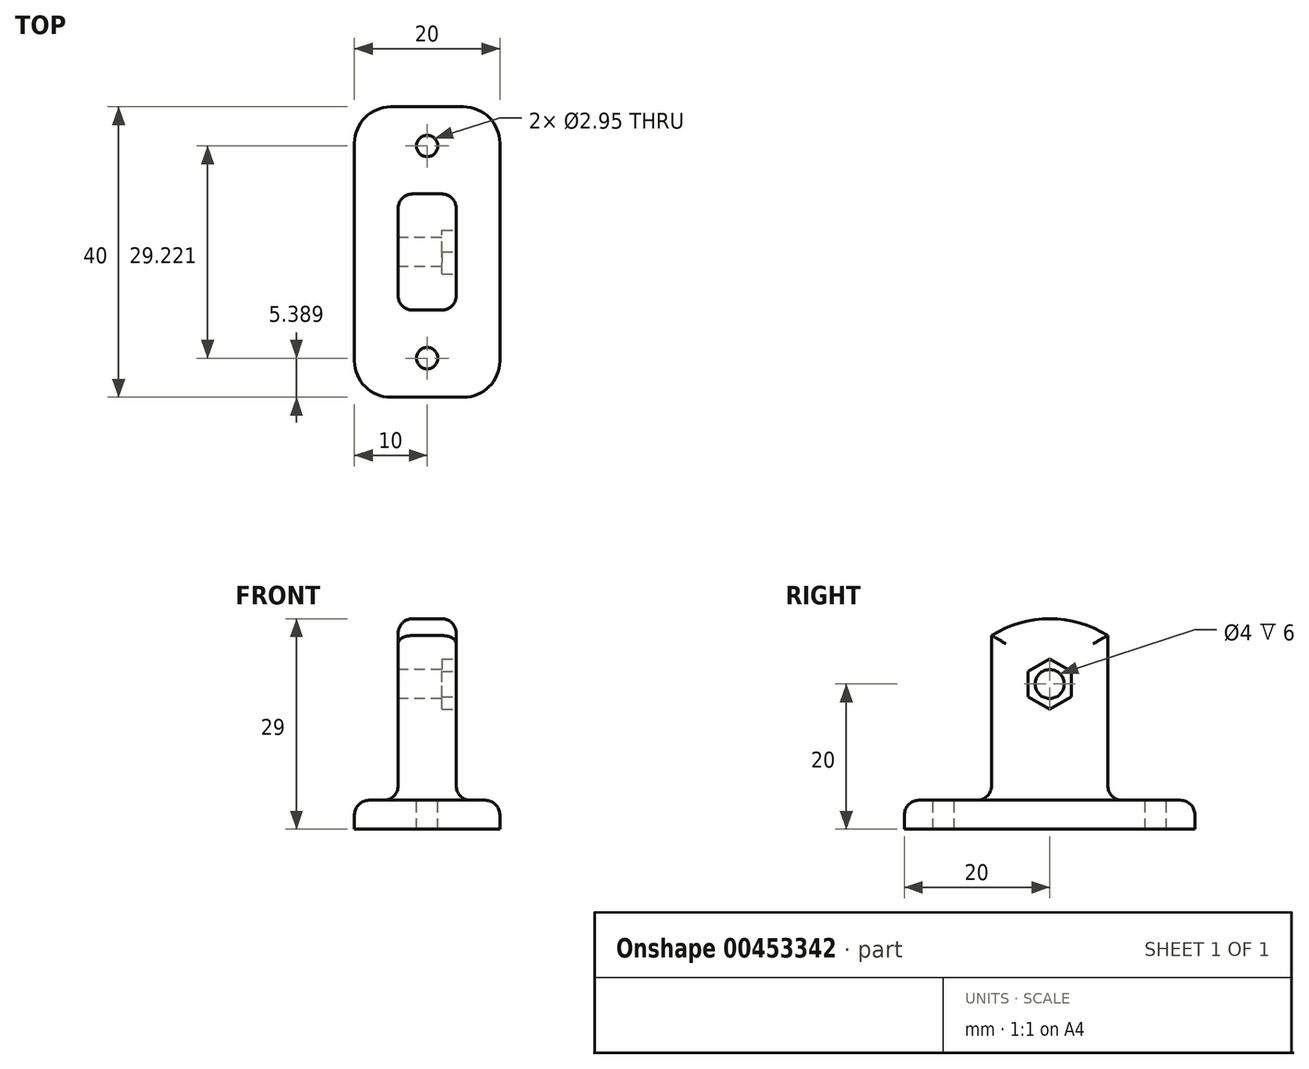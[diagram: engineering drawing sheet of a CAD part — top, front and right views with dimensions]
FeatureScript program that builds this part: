
annotation { "Feature Type Name" : "Feature", "Feature Type Description" : "" }
export const myFeature = defineFeature(function(context is Context, id is Id, definition is map)
    precondition{}
    {
        {
            var Q0;
            Q0=qCreatedBy(makeId("Top.planeOp"),FACE);
            var sketch = newSketch(context, id + "F0", { "sketchPlane" : qUnion([Q0])});
            skLineSegment(sketch, "E0.bottom", {"start": v(10, 20) * mm, "end": v(-10, 20) * mm});
            skLineSegment(sketch, "E0.top", {"start": v(10, -20) * mm, "end": v(-10, -20) * mm});
            skLineSegment(sketch, "E0.left", {"start": v(10, 20) * mm, "end": v(10, -20) * mm});
            skLineSegment(sketch, "E0.right", {"start": v(-10, 20) * mm, "end": v(-10, -20) * mm});
            skPoint(sketch, "E0.middle", {"position": v(0, 0) * mm});
            skSolve(sketch);
        }
        {
            var Q0;
            Q0 = qSketchRegion(id + "F0", true);
            extrude(context, id + "F1", {"entities" : qUnion([Q0]), "depth" : 4 * mm});
        }
        {
            var Q0;
            Q0=makeQuery(id+"F1.opExtrude","CAP_FACE",FACE,{"disambiguationData":[OSD([sQuery(id+"F0.wireOp",EDGE,"E0.bottom"),sQuery(id+"F0.wireOp",EDGE,"E0.top"),sQuery(id+"F0.wireOp",EDGE,"E0.left"),sQuery(id+"F0.wireOp",EDGE,"E0.right")])],"isStart":false});
            var sketch = newSketch(context, id + "F2", { "sketchPlane" : qUnion([Q0])});
            skLineSegment(sketch, "E1.bottom", {"start": v(4, 8) * mm, "end": v(-4, 8) * mm});
            skLineSegment(sketch, "E1.top", {"start": v(4, -8) * mm, "end": v(-4, -8) * mm});
            skLineSegment(sketch, "E1.left", {"start": v(4, 8) * mm, "end": v(4, -8) * mm});
            skLineSegment(sketch, "E1.right", {"start": v(-4, 8) * mm, "end": v(-4, -8) * mm});
            skPoint(sketch, "E1.middle", {"position": v(0, 0) * mm});
            skSolve(sketch);
        }
        {
            var Q0;
            Q0 = qSketchRegion(id + "F2", true);
            extrude(context, id + "F3", {"entities" : qUnion([Q0]), "operationType" : NewBodyOperationType.ADD, "depth" : 25 * mm});
        }
        {
            var Q0;
            Q0=makeQuery(id+"F3.opExtrude","SWEPT_FACE",FACE,{"disambiguationData":[OSD([sQuery(id+"F2.wireOp",EDGE,"E1.left")])]});
            var sketch = newSketch(context, id + "F4", { "sketchPlane" : qUnion([Q0])});
            skCircle(sketch, "E2", {"center": v(0, 14) * mm, "radius": 15 * mm});
            skSolve(sketch);
        }
        {
            var Q0;
            {var subQ0=sQuery(id+"F4.wireOp",EDGE,"E2");var subQ1=sQuery(id+"F2.wireOp",EDGE,"E1.left");var subQ2=makeQuery(id+"F3.opExtrude","CAP_EDGE",EDGE,{"disambiguationData":[OSD([subQ1])],"isStart":false});var subQ3=makeQuery(id+"F4.imprint","INTERSECT",VERTEX,{"derivedFrom":[subQ2,subQ0]});Q0=makeQuery(id+"F4.imprint","IMPRINT",FACE,{"disambiguationData":[TD([[makeQuery(id+"F4.imprint","IMPRINT",EDGE,{"disambiguationData":[TD([[subQ3,-1.0]])],"derivedFrom":subQ0}),-1.0]])]});}
            var Q1;
            {var subQ0=sQuery(id+"F4.wireOp",EDGE,"E2");var subQ1=sQuery(id+"F2.wireOp",EDGE,"E1.left");var subQ2=makeQuery(id+"F3.opExtrude","CAP_EDGE",EDGE,{"disambiguationData":[OSD([subQ1])],"isStart":false});var subQ3=makeQuery(id+"F4.imprint","INTERSECT",VERTEX,{"derivedFrom":[subQ2,subQ0]});Q1=makeQuery(id+"F4.imprint","IMPRINT",FACE,{"disambiguationData":[TD([[makeQuery(id+"F4.imprint","IMPRINT",EDGE,{"disambiguationData":[TD([[subQ3,1.0]])],"derivedFrom":subQ0}),-1.0]])]});}
            extrude(context, id + "F5", {"entities" : qUnion([Q0, Q1]), "operationType" : NewBodyOperationType.REMOVE, "oppositeDirection" : true, "depth" : 25 * mm});
        }
        {
            var Q0;
            Q0=makeQuery(id+"F1.opExtrude","SWEPT_EDGE",EDGE,{"disambiguationData":[OSD([sQuery(id+"F0.wireOp",EDGE,"E0.bottom"),sQuery(id+"F0.wireOp",EDGE,"E0.right")])]});
            var Q1;
            Q1=makeQuery(id+"F1.opExtrude","SWEPT_EDGE",EDGE,{"disambiguationData":[OSD([sQuery(id+"F0.wireOp",EDGE,"E0.top"),sQuery(id+"F0.wireOp",EDGE,"E0.right")])]});
            var Q2;
            Q2=makeQuery(id+"F1.opExtrude","SWEPT_EDGE",EDGE,{"disambiguationData":[OSD([sQuery(id+"F0.wireOp",EDGE,"E0.top"),sQuery(id+"F0.wireOp",EDGE,"E0.left")])]});
            var Q3;
            Q3=makeQuery(id+"F1.opExtrude","SWEPT_EDGE",EDGE,{"disambiguationData":[OSD([sQuery(id+"F0.wireOp",EDGE,"E0.bottom"),sQuery(id+"F0.wireOp",EDGE,"E0.left")])]});
            fillet(context, id + "F6", {"entities" : qUnion([Q0, Q1, Q2, Q3]), "radius" : 5 * mm, "tangentPropagation" : true, "allowEdgeOverflow" : false});
        }
        {
            var Q0;
            Q0=makeQuery(id+"F1.opExtrude","CAP_FACE",FACE,{"disambiguationData":[OSD([sQuery(id+"F0.wireOp",EDGE,"E0.bottom"),sQuery(id+"F0.wireOp",EDGE,"E0.top"),sQuery(id+"F0.wireOp",EDGE,"E0.left"),sQuery(id+"F0.wireOp",EDGE,"E0.right")])],"isStart":false});
            var Q1;
            Q1=makeQuery(id+"F3.opExtrude","SWEPT_FACE",FACE,{"disambiguationData":[OSD([sQuery(id+"F2.wireOp",EDGE,"E1.left")])]});
            var Q2;
            Q2=makeQuery(id+"F3.opExtrude","SWEPT_FACE",FACE,{"disambiguationData":[OSD([sQuery(id+"F2.wireOp",EDGE,"E1.right")])]});
            fillet(context, id + "F7", {"entities" : qUnion([Q0, Q1, Q2]), "radius" : 2 * mm, "tangentPropagation" : true, "allowEdgeOverflow" : false});
        }
        {
            var Q0;
            Q0=makeQuery(id+"F3.opExtrude","SWEPT_FACE",FACE,{"disambiguationData":[OSD([sQuery(id+"F2.wireOp",EDGE,"E1.right")])]});
            var sketch = newSketch(context, id + "F8", { "sketchPlane" : qUnion([Q0])});
            skCircle(sketch, "E3", {"center": v(0, 20) * mm, "radius": 2 * mm});
            skSolve(sketch);
        }
        {
            var Q0;
            Q0=makeQuery(id+"F8.imprint","IMPRINT",FACE,{"disambiguationData":[TD([[makeQuery(id+"F8.imprint","IMPRINT",EDGE,{"derivedFrom":sQuery(id+"F8.wireOp",EDGE,"E3")}),1.0]])]});
            extrude(context, id + "F9", {"entities" : qUnion([Q0]), "operationType" : NewBodyOperationType.REMOVE, "oppositeDirection" : true, "depth" : 25 * mm});
        }
        {
            var Q0;
            Q0=makeQuery(id+"F1.opExtrude","CAP_FACE",FACE,{"disambiguationData":[OSD([sQuery(id+"F0.wireOp",EDGE,"E0.bottom"),sQuery(id+"F0.wireOp",EDGE,"E0.top"),sQuery(id+"F0.wireOp",EDGE,"E0.left"),sQuery(id+"F0.wireOp",EDGE,"E0.right")])],"isStart":false});
            var sketch = newSketch(context, id + "F10", { "sketchPlane" : qUnion([Q0])});
            skLineSegment(sketch, "E4", {"start": v(-24.27, 0) * mm, "end": v(23.68, 0) * mm, "construction": true});
            skCircle(sketch, "E5", {"center": v(0, 14.61) * mm, "radius": 1.47 * mm});
            skCircle(sketch, "E6.MirrorC", {"center": v(0, -14.61) * mm, "radius": 1.47 * mm});
            skSolve(sketch);
        }
        {
            var Q0;
            Q0 = qSketchRegion(id + "F10", true);
            extrude(context, id + "F11", {"entities" : qUnion([Q0]), "operationType" : NewBodyOperationType.REMOVE, "oppositeDirection" : true, "depth" : 5 * mm});
        }
        {
            var Q0;
            Q0=makeQuery(id+"F3.opExtrude","SWEPT_FACE",FACE,{"disambiguationData":[OSD([sQuery(id+"F2.wireOp",EDGE,"E1.left")])]});
            var sketch = newSketch(context, id + "F12", { "sketchPlane" : qUnion([Q0])});
            skCircle(sketch, "E7.cCircle", {"center": v(0, 20) * mm, "radius": 3.46 * mm, "construction": true});
            skLineSegment(sketch, "E7.0", {"start": v(0, 23.46) * mm, "end": v(3, 21.73) * mm});
            skLineSegment(sketch, "E7.1", {"start": v(3, 21.73) * mm, "end": v(3, 18.27) * mm});
            skLineSegment(sketch, "E7.2", {"start": v(3, 18.27) * mm, "end": v(0, 16.54) * mm});
            skLineSegment(sketch, "E7.3", {"start": v(0, 16.54) * mm, "end": v(-3, 18.27) * mm});
            skLineSegment(sketch, "E7.4", {"start": v(-3, 18.27) * mm, "end": v(-3, 21.73) * mm});
            skLineSegment(sketch, "E7.5", {"start": v(-3, 21.73) * mm, "end": v(0, 23.46) * mm});
            skSolve(sketch);
        }
        {
            var Q0;
            Q0 = qSketchRegion(id + "F12", true);
            extrude(context, id + "F13", {"entities" : qUnion([Q0]), "operationType" : NewBodyOperationType.REMOVE, "oppositeDirection" : true, "depth" : 2 * mm});
        }
    });
